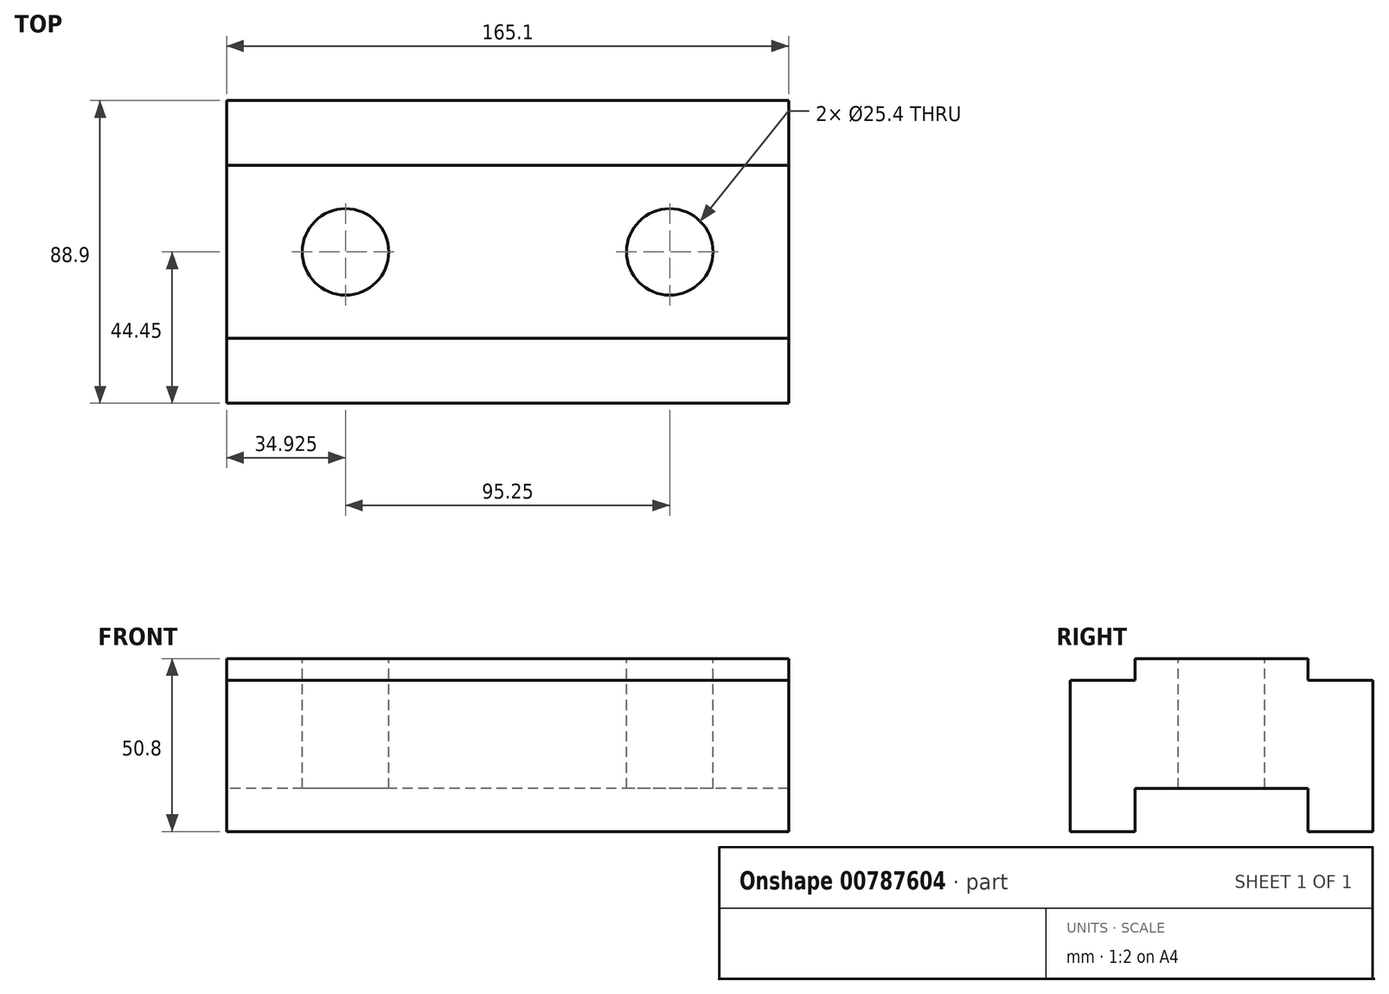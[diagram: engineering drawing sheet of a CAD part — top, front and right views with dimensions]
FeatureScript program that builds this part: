
annotation { "Feature Type Name" : "Feature", "Feature Type Description" : "" }
export const myFeature = defineFeature(function(context is Context, id is Id, definition is map)
    precondition{}
    {
        {
            var Q0;
            Q0=qCreatedBy(makeId("Right.planeOp"),FACE);
            var sketch = newSketch(context, id + "F0", { "sketchPlane" : qUnion([Q0])});
            skLineSegment(sketch, "E0", {"start": v(0, 0) * mm, "end": v(19.05, 0) * mm});
            skLineSegment(sketch, "E1", {"start": v(19.05, 0) * mm, "end": v(19.05, 12.7) * mm});
            skLineSegment(sketch, "E2", {"start": v(19.05, 12.7) * mm, "end": v(69.85, 12.7) * mm});
            skLineSegment(sketch, "E3", {"start": v(69.85, 12.7) * mm, "end": v(69.85, 0) * mm});
            skLineSegment(sketch, "E4", {"start": v(69.85, 0) * mm, "end": v(88.9, 0) * mm});
            skLineSegment(sketch, "E5", {"start": v(88.9, 0) * mm, "end": v(88.9, 44.45) * mm});
            skLineSegment(sketch, "E6", {"start": v(88.9, 44.45) * mm, "end": v(69.85, 44.45) * mm});
            skLineSegment(sketch, "E7", {"start": v(69.85, 44.45) * mm, "end": v(69.85, 50.8) * mm});
            skLineSegment(sketch, "E8", {"start": v(69.85, 50.8) * mm, "end": v(19.05, 50.8) * mm});
            skLineSegment(sketch, "E9", {"start": v(19.05, 50.8) * mm, "end": v(19.05, 44.45) * mm});
            skLineSegment(sketch, "E10", {"start": v(19.05, 44.45) * mm, "end": v(0, 44.45) * mm});
            skLineSegment(sketch, "E11", {"start": v(0, 44.45) * mm, "end": v(0, 0) * mm});
            skSolve(sketch);
        }
        {
            var Q0;
            Q0 = qSketchRegion(id + "F0", true);
            extrude(context, id + "F1", {"entities" : qUnion([Q0]), "depth" : 165.1 * mm, "offsetDistance" : 25.4 * mm});
        }
        {
            var Q0;
            Q0=makeQuery(id+"F1.opExtrude","SWEPT_FACE",FACE,{"disambiguationData":[OSD([sQuery(id+"F0.wireOp",EDGE,"E8")])]});
            var sketch = newSketch(context, id + "F2", { "sketchPlane" : qUnion([Q0])});
            skLineSegment(sketch, "E12", {"start": v(0, 44.45) * mm, "end": v(34.93, 44.45) * mm, "construction": true});
            skLineSegment(sketch, "E13", {"start": v(34.93, 44.45) * mm, "end": v(130.18, 44.45) * mm, "construction": true});
            skCircle(sketch, "E14", {"center": v(34.93, 44.45) * mm, "radius": 12.7 * mm});
            skCircle(sketch, "E15", {"center": v(130.18, 44.45) * mm, "radius": 12.7 * mm});
            skSolve(sketch);
        }
        {
            var Q0;
            Q0 = qSketchRegion(id + "F2", true);
            extrude(context, id + "F3", {"entities" : qUnion([Q0]), "operationType" : NewBodyOperationType.REMOVE, "endBound" : BoundingType.THROUGH_ALL, "oppositeDirection" : true, "depth" : 25.4 * mm, "offsetDistance" : 25.4 * mm});
        }
    });
